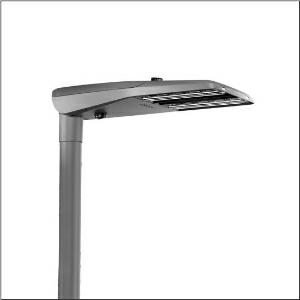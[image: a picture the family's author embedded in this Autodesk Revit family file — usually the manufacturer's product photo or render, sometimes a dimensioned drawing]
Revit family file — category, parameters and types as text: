
# Revit family: streetlight_sl_11_iq_midi___st1_2a_5xc3a61y08me_9d9d
name_source: partatom
category: Lighting Fixtures
units: mm (PartAtom-declared; Revit-internal decimal feet)

## family parameters
Cut with Voids When Loaded = No
Host = Face
Light Source = No
Part Type = Normal
Room Calculation Point = No
Round Connector Dimension = Use Diameter
Shared = No

## types (1)
- --- (1 x LED, 16240 lm, 122.7 W, 2700K)
    Apparent Load = 123 VA
    CIE Flux Codes = 32 70 96 100 100
    Color Rendering = 70
    Color Temperature = 2700K
    Default Elevation = 1800 mm
    Description = Streetlight SL 11 iQ midi, mast luminaire, primary light control with 3 zone facetted reflector, of plastic, silver coated, highly specular, primary optical cover: cover, of PMMA, transparent, light distribution: ST1.2a, light emission: direct distribution, primary light characteristic: asymmetric, installation type: post-top, side-entry, lamps: LED, High Power LED, rated values: 16.240lm | 122,7W | 132,4lm/W (begin service life); end service life: 16.240lm | 130,2W; at 50% lumin. flux: 8.120lm | 56,1W | 144,7lm/W, colour temperature: 2700K, colour rendering: CRI > 70, light colour: 727, light setting 1 begin service life: 100% | 16.240lm | 122,7W | 132,4lm/W | 2.700K, light setting 1 end service life: 130,2W, further light settings possible, control: pre-setting: logarithmic dimming characteristic, Street-Remote, Auto-Match, Temp-Guard, Lumen-Switch, Night-Set, Smart-Wire, Light-Fading, Desk-Remote (wireless, voltage-free reading and setting of iQ features in the workshop via application-optimized NFC function/RFID function), optimised constant luminous flux control (CLO 2.0), with cable H07RN-F 3x 1.5mm², mains connection: 230..240V, AC, 50/60Hz, connection cable pre-assembled, cable length: 12,5m, luminaire housing, of diecast aluminium, powder-coated, SITECO metallic grey (DB 702S), please order mast flange separately, inclination adjustable without tools: 0°, 5°, 10°, 15° (post-top) | 0°, -5°, -10°, -15° (side-entry), sealing non-destructively replaceable, multi-level sealing system, length: 780mm, width: 376mm, height: 118mm, mast flange for spigot size: 42mm (side-entry): 5XC10008XM4, 60/48mm (side-entry/post-top): 5XC10108XM2, 76/60mm (side-entry/post-top): 5XC10108XM1, equipment: Power, Smart Interface below and above, protection rating (complete): IP66, insulation class (complete): insulation class II (safety insulation), certification: CE, ENEC, ENEC+, VDE, UKCA, impact resistance: IK10, permissible operating ambient temperature for outdoor applications: -25..+50°C, standard-compliant lighting for roads and squares, Environmental Product Declaration (EPD) tested and certified by an independent institute, packaging unit: 1 piece

Light Distribution: ST1.2a
    Height = 118 mm
    Lamp = 1 x LED
    Lamp Light Flux = 16240 lm
    Lamp Power = 122.7 W
    Lamp count = 1
    Length = 780 mm
    Luminous efficacy = 132 lm/W
    Manufacturer = Siteco
    ModVariant = No
    Model = 5XC3A61Y08ME
    Number of Poles = 1
    OnlyDefault = Yes
    Power Factor = 1
    Product Name = Streetlight SL 11 iQ midi | ST1.2a
    Product group = mast luminaire | pylon top
    ProductGroupID = 6100
    Protection Class = Protection class II
    Protection Degree = IP 66
    RLX_Detail_Level = 1
    RLX_Emergency_Light_Flux = 0 lm
    RLX_Emergency_Type = 0
    RLX_Emergency_Type_DB = No
    RlxData = <blob elided: 69965 chars, md5=28761394>
    Socket = socket
    Standby Power = 0 W
    System Light Flux = 16241 lm
    System Power = 123 W
    Type Comments = factory setting: luminous flux: 100 % | dim-lin: 254 | 553 mA
    Type Image = l_1004429.jpg
    URL = http://relux.com
    VarID = @adj_132575
    Voltage = 0 V
    Weight = 0.00 kg
    Width = 376 mm

## geometry (parser evidence)
native form markers: Blend x4, Sweep x9
no freeform markers — native parametric forms only
